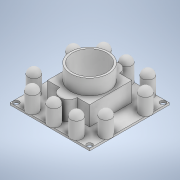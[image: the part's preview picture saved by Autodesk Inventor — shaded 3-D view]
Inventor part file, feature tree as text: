
AUTODESK INVENTOR PART (.ipt)
format: ipt  version: 2020 (Build 240168000, 168)  size: 294,400 bytes
history: native  units: in
note: dims shown in document units (in); Inventor stores cm internally (conversion verified against a paired STEP export)
features: sketch x13, extrude x10, fillet x1
ambient origin geometry x8: Origin, YZ Plane, XZ Plane, XY Plane, X Axis, Y Axis, Z Axis, Center Point
bodies: Solid1 (feature_tree)
feature tree (24):
  extrude  "Extrusion1"  Depth=1.2598in
  extrude  "Extrusion2"  Depth=0.6693in
  extrude  "Extrusion3"  Depth=0.6693in
  extrude  "Extrusion4"  Depth=0.3051in TaperAngle=0.0deg
  sketch  "Sketch5"  dims[d10=0.6031in d11=0.2429in d12=0.0in]
  sketch  "Sketch6"  dims[d13=0.5394in d14=0.548in d15=0.0in]
  sketch  "Sketch7"  dims[d23=0.0874in d24=0.0874in d26=0.0488in]
  sketch  "Sketch8"  dims[d28=0.0488in d29=0.0488in d30=0.0874in]
  extrude  "Extrusion5"  Depth=0.2429in TaperAngle=0.0deg
  sketch  "Sketch9"  dims[d31=0.0874in d32=0.0335in d33=0.0in]
  sketch  "Sketch10"  dims[d34=0.1811in d35=0.0591in]
  extrude  "Extrusion6"  Depth=0.548in TaperAngle=0.0deg
  extrude  "Extrusion7"  Depth=0.0874in
  extrude  "Extrusion8"  Depth=0.0488in
  fillet  "Fillet1"  Radius=0.0874in
  extrude  "Extrusion9"  Depth=0.0335in TaperAngle=0.0deg
  extrude  "Extrusion10"  Depth=0.0591in
  sketch  "Sketch1"  dims[d0=1.2598in d1=1.2598in]
  sketch  "Sketch2"  dims[d2=0.0335in d3=0.0in d4=0.6693in]
  sketch  "Sketch3"  dims[d5=0.6693in d6=0.2756in]
  sketch  "Sketch4"  dims[d7=0.2756in d8=0.3051in d9=0.0in]
  sketch  "Sketch11"  dims[d36=0.2795in]
  sketch  "Sketch12"  dims[d37=0.1811in d38=0.0591in]
  sketch  "Sketch13"  dims[d39=0.2795in d40=0.1811in d41=0.0512in d42=0.6299in d43=0.1811in d44=0.1811in d45=0.1811in d46=0.1811in d47=0.1811in d48=0.1811in d49=0.1811in d50=0.3165in d51=0.0591in d52=0.3165in d53=0.0591in d54=0.3165in d55=0.0591in d56=0.0591in d57=0.3165in d58=0.2795in d59=0.0709in d60=0.2795in d61=0.0709in d62=0.6299in d63=0.063in d64=0.3543in d65=0.0in d66=0.3543in d67=0.0in d68=0.3543in d69=0.0in d70=0.0906in d71=0.1457in d72=0.2913in d73=0.0in d74=0.4843in d75=0.1752in d76=0.0in d77=0.122in d78=0.2677in d79=0.0118in d80=0.0118in d81=0.1732in d82=0.0in]
